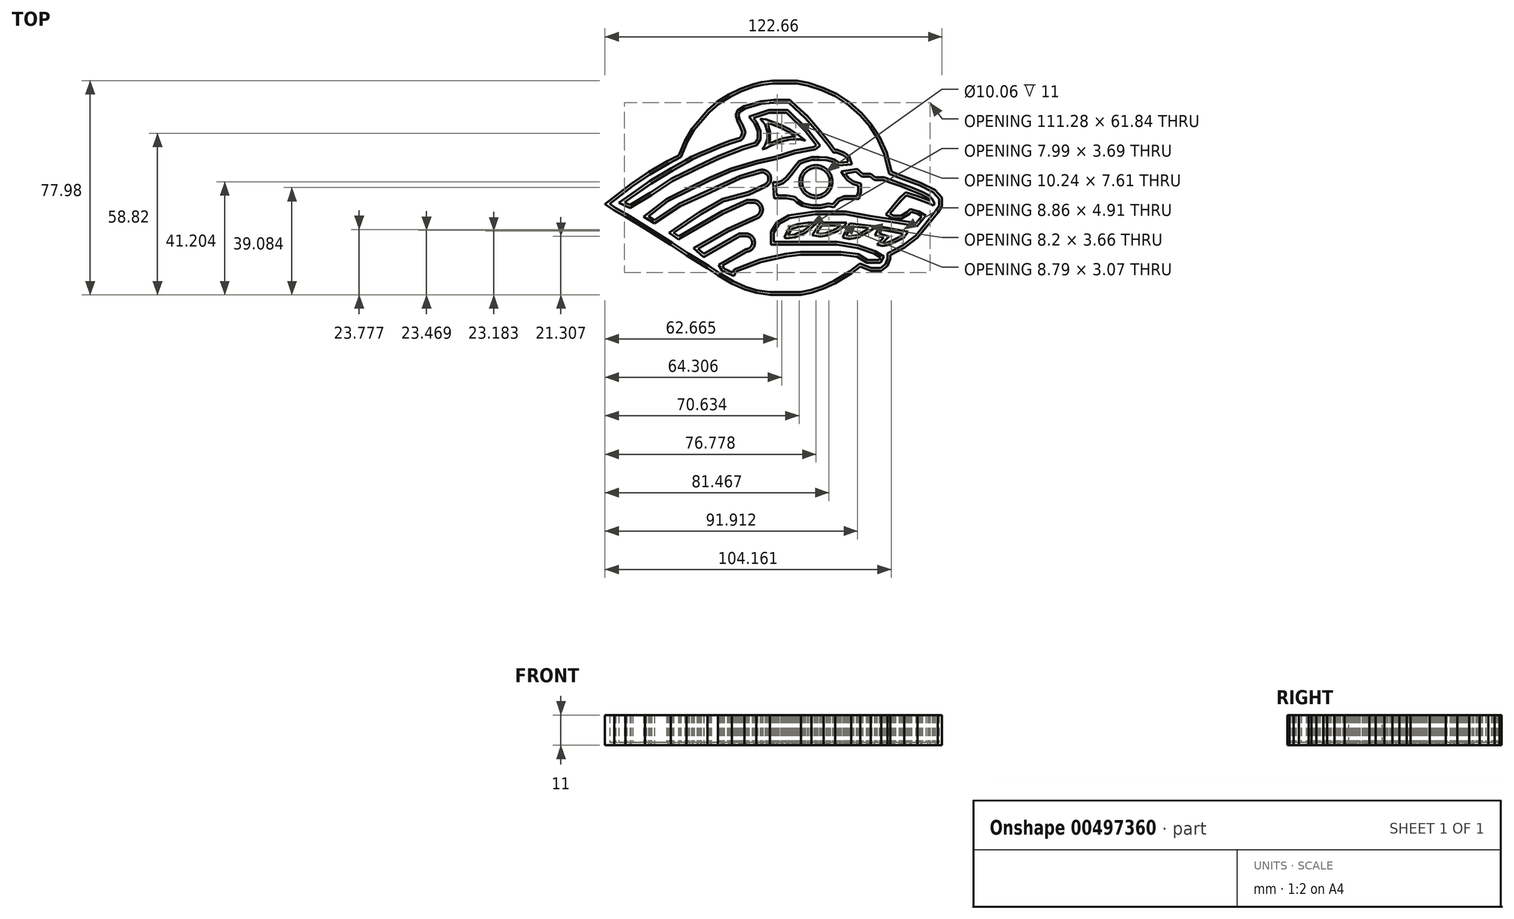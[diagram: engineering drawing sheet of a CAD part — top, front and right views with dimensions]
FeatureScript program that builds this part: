
annotation { "Feature Type Name" : "Feature", "Feature Type Description" : "" }
export const myFeature = defineFeature(function(context is Context, id is Id, definition is map)
    precondition{}
    {
        {
            var Q0;
            Q0=qCreatedBy(makeId("Top.planeOp"),FACE);
            var sketch = newSketch(context, id + "F0", { "sketchPlane" : qUnion([Q0])});
            skLineSegment(sketch, "E0", {"start": v(-64.4, -1.88) * mm, "end": v(-56.05, 4.66) * mm});
            skLineSegment(sketch, "E1", {"start": v(-56.05, 4.66) * mm, "end": v(-49.76, 8.87) * mm});
            skLineSegment(sketch, "E2", {"start": v(-49.76, 8.87) * mm, "end": v(-42.78, 12.9) * mm});
            skLineSegment(sketch, "E3", {"start": v(-42.78, 12.9) * mm, "end": v(-38.45, 15.16) * mm});
            skLineSegment(sketch, "E4", {"start": v(-38.45, 15.16) * mm, "end": v(-36.18, 20.62) * mm});
            skLineSegment(sketch, "E5", {"start": v(-36.18, 20.62) * mm, "end": v(-33.6, 25.09) * mm});
            skLineSegment(sketch, "E6", {"start": v(-33.6, 25.09) * mm, "end": v(-28.15, 31.5) * mm});
            skLineSegment(sketch, "E7", {"start": v(-28.15, 31.5) * mm, "end": v(-24.6, 34.58) * mm});
            skLineSegment(sketch, "E8", {"start": v(-24.6, 34.58) * mm, "end": v(-20.43, 37.2) * mm});
            skLineSegment(sketch, "E9", {"start": v(-20.43, 37.2) * mm, "end": v(-16.4, 39.2) * mm});
            skLineSegment(sketch, "E10", {"start": v(-16.4, 39.2) * mm, "end": v(-11.8, 40.82) * mm});
            skLineSegment(sketch, "E11", {"start": v(-11.8, 40.82) * mm, "end": v(-8.9, 41.51) * mm});
            skLineSegment(sketch, "E12", {"start": v(-8.9, 41.51) * mm, "end": v(-5.07, 42) * mm});
            skLineSegment(sketch, "E13", {"start": v(-5.07, 42) * mm, "end": v(0, 42) * mm});
            skLineSegment(sketch, "E14", {"start": v(0, 42) * mm, "end": v(3.77, 42) * mm});
            skLineSegment(sketch, "E15", {"start": v(3.77, 42) * mm, "end": v(7.58, 41.25) * mm});
            skLineSegment(sketch, "E16", {"start": v(7.58, 41.25) * mm, "end": v(12.68, 39.55) * mm});
            skLineSegment(sketch, "E17", {"start": v(12.68, 39.55) * mm, "end": v(17.83, 37.29) * mm});
            skLineSegment(sketch, "E18", {"start": v(17.83, 37.29) * mm, "end": v(22.37, 34.25) * mm});
            skLineSegment(sketch, "E19", {"start": v(22.37, 34.25) * mm, "end": v(26.64, 30.49) * mm});
            skLineSegment(sketch, "E20", {"start": v(26.64, 30.49) * mm, "end": v(30.21, 26.3) * mm});
            skLineSegment(sketch, "E21", {"start": v(30.21, 26.3) * mm, "end": v(32.91, 22.22) * mm});
            skLineSegment(sketch, "E22", {"start": v(32.91, 22.22) * mm, "end": v(35.46, 16.47) * mm});
            skLineSegment(sketch, "E23", {"start": v(35.46, 16.47) * mm, "end": v(36.78, 11.36) * mm});
            skLineSegment(sketch, "E24", {"start": v(36.78, 11.36) * mm, "end": v(37.36, 9.1) * mm});
            skLineSegment(sketch, "E25", {"start": v(37.36, 9.1) * mm, "end": v(41.44, 7.5) * mm});
            skLineSegment(sketch, "E26", {"start": v(41.44, 7.5) * mm, "end": v(48.44, 4.87) * mm});
            skLineSegment(sketch, "E27", {"start": v(48.44, 4.87) * mm, "end": v(53.32, 2.4) * mm});
            skLineSegment(sketch, "E28", {"start": v(53.32, 2.4) * mm, "end": v(55.56, 0) * mm});
            skLineSegment(sketch, "E29", {"start": v(55.56, 0) * mm, "end": v(55.56, -2.46) * mm});
            skLineSegment(sketch, "E30", {"start": v(55.56, -2.46) * mm, "end": v(54.15, -4.5) * mm});
            skLineSegment(sketch, "E31", {"start": v(54.15, -4.5) * mm, "end": v(49.78, -9.92) * mm});
            skLineSegment(sketch, "E32", {"start": v(49.78, -9.92) * mm, "end": v(46.97, -13.37) * mm});
            skLineSegment(sketch, "E33", {"start": v(46.97, -13.37) * mm, "end": v(42.25, -16.98) * mm});
            skLineSegment(sketch, "E34", {"start": v(42.25, -16.98) * mm, "end": v(36.78, -19.86) * mm});
            skLineSegment(sketch, "E35", {"start": v(36.78, -19.86) * mm, "end": v(36.78, -21.72) * mm});
            skLineSegment(sketch, "E36", {"start": v(36.78, -21.72) * mm, "end": v(35.95, -23.82) * mm});
            skLineSegment(sketch, "E37", {"start": v(35.95, -23.82) * mm, "end": v(34.14, -25.2) * mm});
            skLineSegment(sketch, "E38", {"start": v(34.14, -25.2) * mm, "end": v(30.8, -25.2) * mm});
            skLineSegment(sketch, "E39", {"start": v(30.8, -25.2) * mm, "end": v(26.64, -23.56) * mm});
            skLineSegment(sketch, "E40", {"start": v(26.64, -23.56) * mm, "end": v(22.9, -26.43) * mm});
            skLineSegment(sketch, "E41", {"start": v(22.9, -26.43) * mm, "end": v(17.22, -29.9) * mm});
            skLineSegment(sketch, "E42", {"start": v(17.22, -29.9) * mm, "end": v(13.15, -31.77) * mm});
            skLineSegment(sketch, "E43", {"start": v(13.15, -31.77) * mm, "end": v(8.8, -33.2) * mm});
            skLineSegment(sketch, "E44", {"start": v(8.8, -33.2) * mm, "end": v(5.08, -33.98) * mm});
            skLineSegment(sketch, "E45", {"start": v(5.08, -33.98) * mm, "end": v(3.36, -33.98) * mm});
            skLineSegment(sketch, "E46", {"start": v(3.36, -33.98) * mm, "end": v(0, -33.98) * mm});
            skLineSegment(sketch, "E47", {"start": v(0, -33.98) * mm, "end": v(-6.07, -33.98) * mm});
            skLineSegment(sketch, "E48", {"start": v(-6.07, -33.98) * mm, "end": v(-10.85, -33.27) * mm});
            skLineSegment(sketch, "E49", {"start": v(-10.85, -33.27) * mm, "end": v(-15, -32.05) * mm});
            skLineSegment(sketch, "E50", {"start": v(-15, -32.05) * mm, "end": v(-19.43, -30.05) * mm});
            skLineSegment(sketch, "E51", {"start": v(-19.43, -30.05) * mm, "end": v(-24.43, -27.05) * mm});
            skLineSegment(sketch, "E52", {"start": v(-24.43, -27.05) * mm, "end": v(-28.28, -24.48) * mm});
            skLineSegment(sketch, "E53", {"start": v(-28.28, -24.48) * mm, "end": v(-35.86, -19.84) * mm});
            skLineSegment(sketch, "E54", {"start": v(-35.86, -19.84) * mm, "end": v(-41.56, -16.03) * mm});
            skLineSegment(sketch, "E55", {"start": v(-41.56, -16.03) * mm, "end": v(-51.02, -10.02) * mm});
            skLineSegment(sketch, "E56", {"start": v(-51.02, -10.02) * mm, "end": v(-58.15, -5.7) * mm});
            skLineSegment(sketch, "E57", {"start": v(-58.15, -5.7) * mm, "end": v(-62.23, -3.37) * mm});
            skLineSegment(sketch, "E58", {"start": v(-62.23, -3.37) * mm, "end": v(-64.4, -1.88) * mm});
            skLineSegment(sketch, "E59", {"start": v(-56.97, -3.37) * mm, "end": v(-49.14, 1.4) * mm});
            skPoint(sketch, "E59.endSnap0", {"position": v(-60.23, 1.4) * mm});
            skLineSegment(sketch, "E60", {"start": v(-49.14, 1.4) * mm, "end": v(-41.56, 6.47) * mm});
            skLineSegment(sketch, "E61", {"start": v(-41.56, 6.47) * mm, "end": v(-32.22, 11.03) * mm});
            skLineSegment(sketch, "E62", {"start": v(-32.22, 11.03) * mm, "end": v(-24.43, 14.66) * mm});
            skLineSegment(sketch, "E63", {"start": v(-24.43, 14.66) * mm, "end": v(-15.86, 18.02) * mm});
            skLineSegment(sketch, "E64", {"start": v(-15.86, 18.02) * mm, "end": v(-10.85, 19.56) * mm});
            skLineSegment(sketch, "E65", {"start": v(-10.85, 19.56) * mm, "end": v(-9.56, 21.7) * mm});
            skLineSegment(sketch, "E66", {"start": v(-9.56, 21.7) * mm, "end": v(-9.56, 24.73) * mm});
            skLineSegment(sketch, "E67", {"start": v(-9.56, 24.73) * mm, "end": v(-10.85, 27.94) * mm});
            skLineSegment(sketch, "E68", {"start": v(-10.85, 27.94) * mm, "end": v(-12.02, 29.44) * mm});
            skLineSegment(sketch, "E69", {"start": v(-12.02, 29.44) * mm, "end": v(-6.35, 31.3) * mm});
            skLineSegment(sketch, "E70", {"start": v(-6.35, 31.3) * mm, "end": v(-4.12, 31.3) * mm});
            skLineSegment(sketch, "E71", {"start": v(-4.12, 31.3) * mm, "end": v(0, 31.3) * mm});
            skLineSegment(sketch, "E72", {"start": v(0, 31.3) * mm, "end": v(6.79, 24.73) * mm});
            skLineSegment(sketch, "E73", {"start": v(6.79, 24.73) * mm, "end": v(10.84, 19.56) * mm});
            skLineSegment(sketch, "E74", {"start": v(10.84, 19.56) * mm, "end": v(9.97, 18.88) * mm});
            skLineSegment(sketch, "E75", {"start": v(9.97, 18.88) * mm, "end": v(2.87, 17.6) * mm});
            skLineSegment(sketch, "E76", {"start": v(2.87, 17.6) * mm, "end": v(-4.12, 15.36) * mm});
            skLineSegment(sketch, "E77", {"start": v(-4.12, 15.36) * mm, "end": v(-10.85, 13.82) * mm});
            skLineSegment(sketch, "E78", {"start": v(-10.85, 13.82) * mm, "end": v(-20.33, 11.03) * mm});
            skLineSegment(sketch, "E79", {"start": v(-20.33, 11.03) * mm, "end": v(-28.28, 7.53) * mm});
            skLineSegment(sketch, "E80", {"start": v(-28.28, 7.53) * mm, "end": v(-35.86, 3.9) * mm});
            skLineSegment(sketch, "E81", {"start": v(-35.86, 3.9) * mm, "end": v(-43.68, 0) * mm});
            skLineSegment(sketch, "E82", {"start": v(-43.68, 0) * mm, "end": v(-52.05, -6.54) * mm});
            skLineSegment(sketch, "E83", {"start": v(-52.05, -6.54) * mm, "end": v(-48.07, -8.96) * mm});
            skLineSegment(sketch, "E84", {"start": v(-48.07, -8.96) * mm, "end": v(-38.7, -2.68) * mm});
            skLineSegment(sketch, "E85", {"start": v(-38.7, -2.68) * mm, "end": v(-29.7, 1.4) * mm});
            skLineSegment(sketch, "E86", {"start": v(-29.7, 1.4) * mm, "end": v(-16.7, 7.4) * mm});
            skLineSegment(sketch, "E87", {"start": v(-16.7, 7.4) * mm, "end": v(-9.56, 9.49) * mm});
            skArc(sketch, "E88", {"start": v(-7.9, 5.3) * mm, "mid": v(-6.81, 8.15) * mm, "end": v(-9.56, 9.49) * mm});
            skLineSegment(sketch, "E89", {"start": v(-7.9, 5.3) * mm, "end": v(-14, 2.48) * mm});
            skLineSegment(sketch, "E90", {"start": v(-14, 2.48) * mm, "end": v(-23.41, 0) * mm});
            skLineSegment(sketch, "E91", {"start": v(-23.41, 0) * mm, "end": v(-31.85, -4.87) * mm});
            skLineSegment(sketch, "E92", {"start": v(-31.85, -4.87) * mm, "end": v(-42.85, -12.32) * mm});
            skLineSegment(sketch, "E93", {"start": v(-42.85, -12.32) * mm, "end": v(-39.35, -14.84) * mm});
            skLineSegment(sketch, "E94", {"start": v(-39.35, -14.84) * mm, "end": v(-31.7, -10.43) * mm});
            skLineSegment(sketch, "E95", {"start": v(-31.7, -10.43) * mm, "end": v(-23.02, -5.42) * mm});
            skLineSegment(sketch, "E96", {"start": v(-23.02, -5.42) * mm, "end": v(-14.3, -1.4) * mm});
            skLineSegment(sketch, "E97", {"start": v(-14.3, -1.4) * mm, "end": v(-12.23, -1.4) * mm});
            skArc(sketch, "E98", {"start": v(-10.94, -6.17) * mm, "mid": v(-9.75, -3.3) * mm, "end": v(-12.23, -1.4) * mm});
            skPoint(sketch, "E98.startSnap0", {"position": v(-10.94, 3.89) * mm});
            skLineSegment(sketch, "E99", {"start": v(-10.94, -6.17) * mm, "end": v(-21.6, -10.93) * mm});
            skLineSegment(sketch, "E100", {"start": v(-21.6, -10.93) * mm, "end": v(-33.9, -18.02) * mm});
            skLineSegment(sketch, "E101", {"start": v(-33.9, -18.02) * mm, "end": v(-30.26, -21.27) * mm});
            skLineSegment(sketch, "E102", {"start": v(-30.26, -21.27) * mm, "end": v(-24.16, -17.75) * mm});
            skLineSegment(sketch, "E103", {"start": v(-24.16, -17.75) * mm, "end": v(-16.98, -13.61) * mm});
            skLineSegment(sketch, "E104", {"start": v(-16.98, -13.61) * mm, "end": v(-14.88, -13.61) * mm});
            skArc(sketch, "E105", {"start": v(-14.88, -18.34) * mm, "mid": v(-12.52, -15.98) * mm, "end": v(-14.88, -13.61) * mm});
            skLineSegment(sketch, "E106", {"start": v(-14.88, -18.34) * mm, "end": v(-24.7, -24) * mm});
            skLineSegment(sketch, "E107", {"start": v(-24.7, -24) * mm, "end": v(-23.43, -26.2) * mm});
            skLineSegment(sketch, "E108", {"start": v(-23.43, -26.2) * mm, "end": v(-14.88, -30.05) * mm});
            skLineSegment(sketch, "E109", {"start": v(-14.88, -30.05) * mm, "end": v(-8.45, -32.05) * mm});
            skLineSegment(sketch, "E110", {"start": v(-8.45, -32.05) * mm, "end": v(-2.72, -32.05) * mm});
            skLineSegment(sketch, "E111", {"start": v(-2.72, -32.05) * mm, "end": v(0, -32.05) * mm});
            skLineSegment(sketch, "E112", {"start": v(0, -32.05) * mm, "end": v(6.1, -32.05) * mm});
            skLineSegment(sketch, "E113", {"start": v(6.1, -32.05) * mm, "end": v(13.7, -28.6) * mm});
            skLineSegment(sketch, "E114", {"start": v(13.7, -28.6) * mm, "end": v(22.13, -23.75) * mm});
            skLineSegment(sketch, "E115", {"start": v(22.13, -23.75) * mm, "end": v(25.67, -21.13) * mm});
            skLineSegment(sketch, "E116", {"start": v(25.67, -21.13) * mm, "end": v(29.22, -23.27) * mm});
            skLineSegment(sketch, "E117", {"start": v(29.22, -23.27) * mm, "end": v(34.2, -23.27) * mm});
            skLineSegment(sketch, "E118", {"start": v(34.2, -23.27) * mm, "end": v(35.52, -21.06) * mm});
            skLineSegment(sketch, "E119", {"start": v(35.52, -21.06) * mm, "end": v(32.31, -19.14) * mm});
            skLineSegment(sketch, "E120", {"start": v(32.31, -19.14) * mm, "end": v(26.22, -16.94) * mm});
            skLineSegment(sketch, "E121", {"start": v(26.22, -16.94) * mm, "end": v(18.4, -15.68) * mm});
            skLineSegment(sketch, "E122", {"start": v(18.4, -15.68) * mm, "end": v(9.3, -15.68) * mm});
            skLineSegment(sketch, "E123", {"start": v(9.3, -15.68) * mm, "end": v(1.34, -15.68) * mm});
            skLineSegment(sketch, "E124", {"start": v(1.34, -15.68) * mm, "end": v(-2.44, -15.68) * mm});
            skLineSegment(sketch, "E125", {"start": v(-2.44, -15.68) * mm, "end": v(-4.68, -15.68) * mm});
            skLineSegment(sketch, "E126", {"start": v(-4.68, -15.68) * mm, "end": v(-4.68, -12.32) * mm});
            skLineSegment(sketch, "E127", {"start": v(-4.68, -12.32) * mm, "end": v(-2.82, -9.24) * mm});
            skLineSegment(sketch, "E128", {"start": v(-2.82, -9.24) * mm, "end": v(1.1, -6.98) * mm});
            skLineSegment(sketch, "E129", {"start": v(1.1, -6.98) * mm, "end": v(10.43, -5.61) * mm});
            skLineSegment(sketch, "E130", {"start": v(10.43, -5.61) * mm, "end": v(21.33, -5.61) * mm});
            skLineSegment(sketch, "E131", {"start": v(21.33, -5.61) * mm, "end": v(30.28, -7.29) * mm});
            skLineSegment(sketch, "E132", {"start": v(30.28, -7.29) * mm, "end": v(40.49, -8.83) * mm});
            skLineSegment(sketch, "E133", {"start": v(40.49, -8.83) * mm, "end": v(47.53, -9.92) * mm});
            skLineSegment(sketch, "E134", {"start": v(47.53, -9.92) * mm, "end": v(50.66, -6.1) * mm});
            skLineSegment(sketch, "E135", {"start": v(50.66, -6.1) * mm, "end": v(48.12, -4.57) * mm});
            skLineSegment(sketch, "E136", {"start": v(48.12, -4.57) * mm, "end": v(44.94, -3.67) * mm});
            skLineSegment(sketch, "E137", {"start": v(44.94, -3.67) * mm, "end": v(44.02, -4.8) * mm});
            skLineSegment(sketch, "E138", {"start": v(44.02, -4.8) * mm, "end": v(41.71, -6.13) * mm});
            skLineSegment(sketch, "E139", {"start": v(41.71, -6.13) * mm, "end": v(40.5, -6.13) * mm});
            skLineSegment(sketch, "E140", {"start": v(40.5, -6.13) * mm, "end": v(38.99, -6.13) * mm});
            skLineSegment(sketch, "E141", {"start": v(38.99, -6.13) * mm, "end": v(37.65, -5.43) * mm});
            skLineSegment(sketch, "E142", {"start": v(37.65, -5.43) * mm, "end": v(41.71, -0.66) * mm});
            skLineSegment(sketch, "E143", {"start": v(41.71, -0.66) * mm, "end": v(43.6, 1.27) * mm});
            skLineSegment(sketch, "E144", {"start": v(43.6, 1.27) * mm, "end": v(47.45, 0) * mm});
            skLineSegment(sketch, "E145", {"start": v(47.45, 0) * mm, "end": v(51.89, -1.66) * mm});
            skLineSegment(sketch, "E146", {"start": v(51.89, -1.66) * mm, "end": v(53.52, -2.46) * mm});
            skLineSegment(sketch, "E147", {"start": v(53.52, -2.46) * mm, "end": v(53.9, -1.66) * mm});
            skLineSegment(sketch, "E148", {"start": v(53.9, -1.66) * mm, "end": v(52.95, 0) * mm});
            skLineSegment(sketch, "E149", {"start": v(52.95, 0) * mm, "end": v(51.89, 1.16) * mm});
            skLineSegment(sketch, "E150", {"start": v(51.89, 1.16) * mm, "end": v(49.39, 2.5) * mm});
            skLineSegment(sketch, "E151", {"start": v(49.39, 2.5) * mm, "end": v(45.53, 4.1) * mm});
            skLineSegment(sketch, "E152", {"start": v(45.53, 4.1) * mm, "end": v(41.71, 5.56) * mm});
            skLineSegment(sketch, "E153", {"start": v(41.71, 5.56) * mm, "end": v(38, 6.89) * mm});
            skLineSegment(sketch, "E154", {"start": v(38, 6.89) * mm, "end": v(35.4, 7.82) * mm});
            skLineSegment(sketch, "E155", {"start": v(35.4, 7.82) * mm, "end": v(34.67, 12.55) * mm});
            skLineSegment(sketch, "E156", {"start": v(34.67, 12.55) * mm, "end": v(33.2, 16.88) * mm});
            skLineSegment(sketch, "E157", {"start": v(33.2, 16.88) * mm, "end": v(31.56, 20.94) * mm});
            skPoint(sketch, "E157.endSnap0", {"position": v(31.56, 24.27) * mm});
            skLineSegment(sketch, "E158", {"start": v(31.56, 20.94) * mm, "end": v(28.02, 26.3) * mm});
            skLineSegment(sketch, "E159", {"start": v(28.02, 26.3) * mm, "end": v(24.44, 30.49) * mm});
            skLineSegment(sketch, "E160", {"start": v(24.44, 30.49) * mm, "end": v(18.81, 34.42) * mm});
            skLineSegment(sketch, "E161", {"start": v(18.81, 34.42) * mm, "end": v(11.34, 38.26) * mm});
            skLineSegment(sketch, "E162", {"start": v(11.34, 38.26) * mm, "end": v(5.52, 39.72) * mm});
            skLineSegment(sketch, "E163", {"start": v(5.52, 39.72) * mm, "end": v(0, 40.65) * mm});
            skLineSegment(sketch, "E164", {"start": v(0, 40.65) * mm, "end": v(-7.35, 39.72) * mm});
            skLineSegment(sketch, "E165", {"start": v(-7.35, 39.72) * mm, "end": v(-13.68, 38.37) * mm});
            skLineSegment(sketch, "E166", {"start": v(-13.68, 38.37) * mm, "end": v(-18.24, 36.5) * mm});
            skLineSegment(sketch, "E167", {"start": v(-18.24, 36.5) * mm, "end": v(-23.7, 33.07) * mm});
            skLineSegment(sketch, "E168", {"start": v(-23.7, 33.07) * mm, "end": v(-28, 28.95) * mm});
            skLineSegment(sketch, "E169", {"start": v(-28, 28.95) * mm, "end": v(-31.22, 25) * mm});
            skLineSegment(sketch, "E170", {"start": v(-31.22, 25) * mm, "end": v(-34.45, 19.63) * mm});
            skLineSegment(sketch, "E171", {"start": v(-34.45, 19.63) * mm, "end": v(-36.78, 13.99) * mm});
            skLineSegment(sketch, "E172", {"start": v(-36.78, 13.99) * mm, "end": v(-41.97, 11.12) * mm});
            skLineSegment(sketch, "E173", {"start": v(-41.97, 11.12) * mm, "end": v(-49.86, 6.37) * mm});
            skLineSegment(sketch, "E174", {"start": v(-49.86, 6.37) * mm, "end": v(-56.94, 1.44) * mm});
            skLineSegment(sketch, "E175", {"start": v(-56.94, 1.44) * mm, "end": v(-61.06, -1.43) * mm});
            skLineSegment(sketch, "E176", {"start": v(-61.06, -1.43) * mm, "end": v(-56.97, -3.37) * mm});
            skLineSegment(sketch, "E177", {"start": v(-3.57, 1.24) * mm, "end": v(0, 1.24) * mm});
            skLineSegment(sketch, "E178", {"start": v(0, 1.24) * mm, "end": v(2.35, 0.8) * mm});
            skLineSegment(sketch, "E179", {"start": v(2.35, 0.8) * mm, "end": v(3.09, 0.66) * mm});
            skLineSegment(sketch, "E180", {"start": v(3.09, 0.66) * mm, "end": v(4.3, -0.56) * mm});
            skLineSegment(sketch, "E181", {"start": v(4.3, -0.56) * mm, "end": v(6.1, -1.7) * mm});
            skLineSegment(sketch, "E182", {"start": v(6.1, -1.7) * mm, "end": v(7.7, -2.01) * mm});
            skLineSegment(sketch, "E183", {"start": v(7.7, -2.01) * mm, "end": v(9.3, -2.3) * mm});
            skLineSegment(sketch, "E184", {"start": v(9.3, -2.3) * mm, "end": v(12.3, -2.3) * mm});
            skLineSegment(sketch, "E185", {"start": v(12.3, -2.3) * mm, "end": v(15.24, -1.7) * mm});
            skLineSegment(sketch, "E186", {"start": v(15.24, -1.7) * mm, "end": v(16.84, -2) * mm});
            skLineSegment(sketch, "E187", {"start": v(16.84, -2) * mm, "end": v(18.57, 0) * mm});
            skLineSegment(sketch, "E188", {"start": v(18.57, 0) * mm, "end": v(20.92, 0.96) * mm});
            skLineSegment(sketch, "E189", {"start": v(20.92, 0.96) * mm, "end": v(23.05, 0.96) * mm});
            skLineSegment(sketch, "E190", {"start": v(23.05, 0.96) * mm, "end": v(25.54, 0.96) * mm});
            skLineSegment(sketch, "E191", {"start": v(25.54, 0.96) * mm, "end": v(26.05, 2.53) * mm});
            skLineSegment(sketch, "E192", {"start": v(26.05, 2.53) * mm, "end": v(26.05, 4.78) * mm});
            skLineSegment(sketch, "E193", {"start": v(26.05, 4.78) * mm, "end": v(24.01, 5.37) * mm});
            skLineSegment(sketch, "E194", {"start": v(24.01, 5.37) * mm, "end": v(21.98, 6.85) * mm});
            skLineSegment(sketch, "E195", {"start": v(21.98, 6.85) * mm, "end": v(20.84, 8.29) * mm});
            skLineSegment(sketch, "E196", {"start": v(20.84, 8.29) * mm, "end": v(19.78, 9.98) * mm});
            skLineSegment(sketch, "E197", {"start": v(19.78, 9.98) * mm, "end": v(18.77, 12.1) * mm});
            skLineSegment(sketch, "E198", {"start": v(18.77, 12.1) * mm, "end": v(17.03, 13.4) * mm});
            skLineSegment(sketch, "E199", {"start": v(17.03, 13.4) * mm, "end": v(14.5, 14.09) * mm});
            skLineSegment(sketch, "E200", {"start": v(14.5, 14.09) * mm, "end": v(11.95, 14.13) * mm});
            skLineSegment(sketch, "E201", {"start": v(11.95, 14.13) * mm, "end": v(9.25, 14.13) * mm});
            skLineSegment(sketch, "E202", {"start": v(9.25, 14.13) * mm, "end": v(6.5, 13.37) * mm});
            skLineSegment(sketch, "E203", {"start": v(6.5, 13.37) * mm, "end": v(5.02, 12.77) * mm});
            skLineSegment(sketch, "E204", {"start": v(5.02, 12.77) * mm, "end": v(3.58, 11.04) * mm});
            skLineSegment(sketch, "E205", {"start": v(3.58, 11.04) * mm, "end": v(1.84, 8.71) * mm});
            skLineSegment(sketch, "E206", {"start": v(1.84, 8.71) * mm, "end": v(0.36, 7.02) * mm});
            skLineSegment(sketch, "E207", {"start": v(0.36, 7.02) * mm, "end": v(-1.29, 5.7) * mm});
            skLineSegment(sketch, "E208", {"start": v(-1.29, 5.7) * mm, "end": v(-2.9, 5.03) * mm});
            skLineSegment(sketch, "E209", {"start": v(-2.9, 5.03) * mm, "end": v(-3.83, 5.03) * mm});
            skLineSegment(sketch, "E210", {"start": v(-3.83, 5.03) * mm, "end": v(-3.57, 1.24) * mm});
            skLineSegment(sketch, "E211", {"start": v(1.1, -10.1) * mm, "end": v(-0.9, -13.97) * mm});
            skLineSegment(sketch, "E212", {"start": v(-0.9, -13.97) * mm, "end": v(0, -14.44) * mm});
            skLineSegment(sketch, "E213", {"start": v(0, -14.44) * mm, "end": v(3.09, -14) * mm});
            skLineSegment(sketch, "E214", {"start": v(3.09, -14) * mm, "end": v(6.83, -12.31) * mm});
            skLineSegment(sketch, "E215", {"start": v(6.83, -12.31) * mm, "end": v(9.3, -10.32) * mm});
            skLineSegment(sketch, "E216", {"start": v(9.3, -10.32) * mm, "end": v(11.03, -8.67) * mm});
            skLineSegment(sketch, "E217", {"start": v(11.03, -8.67) * mm, "end": v(7.82, -8.67) * mm});
            skLineSegment(sketch, "E218", {"start": v(7.82, -8.67) * mm, "end": v(4.27, -9.19) * mm});
            skLineSegment(sketch, "E219", {"start": v(4.27, -9.19) * mm, "end": v(1.1, -10.1) * mm});
            skLineSegment(sketch, "E220", {"start": v(9.3, -13.2) * mm, "end": v(12.3, -8.67) * mm});
            skLineSegment(sketch, "E221", {"start": v(12.3, -8.67) * mm, "end": v(18.4, -8.67) * mm});
            skLineSegment(sketch, "E222", {"start": v(18.4, -8.67) * mm, "end": v(21.86, -8.67) * mm});
            skLineSegment(sketch, "E223", {"start": v(21.86, -8.67) * mm, "end": v(20.87, -10.1) * mm});
            skLineSegment(sketch, "E224", {"start": v(20.87, -10.1) * mm, "end": v(18.4, -11.87) * mm});
            skLineSegment(sketch, "E225", {"start": v(18.4, -11.87) * mm, "end": v(14.57, -13.42) * mm});
            skLineSegment(sketch, "E226", {"start": v(14.57, -13.42) * mm, "end": v(12.3, -13.75) * mm});
            skLineSegment(sketch, "E227", {"start": v(12.3, -13.75) * mm, "end": v(9.3, -13.2) * mm});
            skLineSegment(sketch, "E228", {"start": v(22.97, -8.89) * mm, "end": v(32.8, -10.1) * mm});
            skLineSegment(sketch, "E229", {"start": v(32.8, -10.1) * mm, "end": v(29.5, -12.2) * mm});
            skLineSegment(sketch, "E230", {"start": v(29.5, -12.2) * mm, "end": v(25.95, -14.2) * mm});
            skLineSegment(sketch, "E231", {"start": v(25.95, -14.2) * mm, "end": v(22.9, -14.64) * mm});
            skLineSegment(sketch, "E232", {"start": v(22.9, -14.64) * mm, "end": v(20.5, -14.2) * mm});
            skLineSegment(sketch, "E233", {"start": v(20.5, -14.2) * mm, "end": v(20.69, -13.2) * mm});
            skLineSegment(sketch, "E234", {"start": v(20.69, -13.2) * mm, "end": v(22.97, -8.89) * mm});
            skLineSegment(sketch, "E235", {"start": v(32.15, -13.2) * mm, "end": v(33.91, -10.1) * mm});
            skLineSegment(sketch, "E236", {"start": v(33.91, -10.1) * mm, "end": v(40.8, -11.4) * mm});
            skLineSegment(sketch, "E237", {"start": v(40.8, -11.4) * mm, "end": v(44.25, -12.04) * mm});
            skLineSegment(sketch, "E238", {"start": v(44.25, -12.04) * mm, "end": v(42.65, -14.2) * mm});
            skLineSegment(sketch, "E239", {"start": v(42.65, -14.2) * mm, "end": v(39.66, -15.68) * mm});
            skLineSegment(sketch, "E240", {"start": v(39.66, -15.68) * mm, "end": v(37, -16.85) * mm});
            skLineSegment(sketch, "E241", {"start": v(37, -16.85) * mm, "end": v(35, -17.14) * mm});
            skLineSegment(sketch, "E242", {"start": v(35, -17.14) * mm, "end": v(32.88, -16.74) * mm});
            skLineSegment(sketch, "E243", {"start": v(32.88, -16.74) * mm, "end": v(35.35, -14.2) * mm});
            skLineSegment(sketch, "E244", {"start": v(35.35, -14.2) * mm, "end": v(32.15, -13.2) * mm});
            skCircle(sketch, "E245", {"center": v(10.68, 6.22) * mm, "radius": 6.03 * mm});
            skLineSegment(sketch, "E246", {"start": v(-18.36, -26.52) * mm, "end": v(-9.27, -22.98) * mm});
            skLineSegment(sketch, "E247", {"start": v(-9.27, -22.98) * mm, "end": v(0, -20.97) * mm});
            skLineSegment(sketch, "E248", {"start": v(5.06, -20.36) * mm, "end": v(0, -20.97) * mm});
            skLineSegment(sketch, "E249", {"start": v(5.06, -20.36) * mm, "end": v(12.15, -20.36) * mm});
            skLineSegment(sketch, "E250", {"start": v(12.15, -20.36) * mm, "end": v(19.7, -20.36) * mm});
            skLineSegment(sketch, "E251", {"start": v(19.7, -20.36) * mm, "end": v(25.67, -21.13) * mm});
            skLineSegment(sketch, "E252", {"start": v(35.4, 7.82) * mm, "end": v(32.34, 7.82) * mm});
            skLineSegment(sketch, "E253", {"start": v(32.34, 7.82) * mm, "end": v(30.64, 9.08) * mm});
            skLineSegment(sketch, "E254", {"start": v(30.64, 9.08) * mm, "end": v(27.71, 9.08) * mm});
            skLineSegment(sketch, "E255", {"start": v(27.71, 9.08) * mm, "end": v(25.67, 10.93) * mm});
            skLineSegment(sketch, "E256", {"start": v(25.67, 10.93) * mm, "end": v(23.7, 12.47) * mm});
            skLineSegment(sketch, "E257", {"start": v(23.7, 12.47) * mm, "end": v(22.8, 15.54) * mm});
            skLineSegment(sketch, "E258", {"start": v(22.8, 15.54) * mm, "end": v(20.92, 16.78) * mm});
            skLineSegment(sketch, "E259", {"start": v(20.92, 16.78) * mm, "end": v(18.31, 17.86) * mm});
            skLineSegment(sketch, "E260", {"start": v(18.31, 17.86) * mm, "end": v(17.55, 17.86) * mm});
            skLineSegment(sketch, "E261", {"start": v(17.55, 17.86) * mm, "end": v(15.91, 20.1) * mm});
            skLineSegment(sketch, "E262", {"start": v(15.91, 20.1) * mm, "end": v(12.1, 24.86) * mm});
            skLineSegment(sketch, "E263", {"start": v(12.1, 24.86) * mm, "end": v(7.47, 30.17) * mm});
            skLineSegment(sketch, "E264", {"start": v(7.47, 30.17) * mm, "end": v(3.66, 33.64) * mm});
            skLineSegment(sketch, "E265", {"start": v(3.66, 33.64) * mm, "end": v(1.2, 36.02) * mm});
            skLineSegment(sketch, "E266", {"start": v(1.2, 36.02) * mm, "end": v(-0.9, 36.02) * mm});
            skLineSegment(sketch, "E267", {"start": v(-0.9, 36.02) * mm, "end": v(-4.72, 36.02) * mm});
            skLineSegment(sketch, "E268", {"start": v(-4.72, 36.02) * mm, "end": v(-9.35, 35.55) * mm});
            skLineSegment(sketch, "E269", {"start": v(-9.35, 35.55) * mm, "end": v(-15.47, 33.78) * mm});
            skLineSegment(sketch, "E270", {"start": v(-15.47, 33.78) * mm, "end": v(-17.92, 32.21) * mm});
            skLineSegment(sketch, "E271", {"start": v(-17.92, 32.21) * mm, "end": v(-18.54, 30.37) * mm});
            skLineSegment(sketch, "E272", {"start": v(-18.54, 30.37) * mm, "end": v(-17.92, 28.26) * mm});
            skLineSegment(sketch, "E273", {"start": v(-17.92, 28.26) * mm, "end": v(-16.83, 26.15) * mm});
            skLineSegment(sketch, "E274", {"start": v(-16.83, 26.15) * mm, "end": v(-16.09, 24.18) * mm});
            skLineSegment(sketch, "E275", {"start": v(-16.09, 24.18) * mm, "end": v(-16.56, 22.68) * mm});
            skLineSegment(sketch, "E276", {"start": v(-16.56, 22.68) * mm, "end": v(-17.17, 22.14) * mm});
            skLineSegment(sketch, "E277", {"start": v(-17.17, 22.14) * mm, "end": v(-20.58, 21.11) * mm});
            skLineSegment(sketch, "E278", {"start": v(-20.58, 21.11) * mm, "end": v(-24.19, 19.75) * mm});
            skLineSegment(sketch, "E279", {"start": v(-24.19, 19.75) * mm, "end": v(-27.8, 18.25) * mm});
            skLineSegment(sketch, "E280", {"start": v(-27.8, 18.25) * mm, "end": v(-31.54, 16.76) * mm});
            skLineSegment(sketch, "E281", {"start": v(-31.54, 16.76) * mm, "end": v(-34.6, 15.26) * mm});
            skLineSegment(sketch, "E282", {"start": v(-34.6, 15.26) * mm, "end": v(-36.78, 13.99) * mm});
            skLineSegment(sketch, "E283", {"start": v(-8.85, 17.93) * mm, "end": v(-7.88, 19.57) * mm});
            skLineSegment(sketch, "E284", {"start": v(-7.88, 19.57) * mm, "end": v(-7.03, 21.75) * mm});
            skLineSegment(sketch, "E285", {"start": v(-7.03, 21.75) * mm, "end": v(-7.03, 24.3) * mm});
            skLineSegment(sketch, "E286", {"start": v(-7.03, 24.3) * mm, "end": v(-7.82, 27.15) * mm});
            skLineSegment(sketch, "E287", {"start": v(-7.82, 27.15) * mm, "end": v(-9.7, 29.22) * mm});
            skLineSegment(sketch, "E288", {"start": v(-9.7, 29.22) * mm, "end": v(-7.51, 28.91) * mm});
            skLineSegment(sketch, "E289", {"start": v(-7.51, 28.91) * mm, "end": v(-5.09, 28.06) * mm});
            skLineSegment(sketch, "E290", {"start": v(-5.09, 28.06) * mm, "end": v(-1.75, 26.8) * mm});
            skLineSegment(sketch, "E291", {"start": v(-1.75, 26.8) * mm, "end": v(1.28, 25.21) * mm});
            skLineSegment(sketch, "E292", {"start": v(1.28, 25.21) * mm, "end": v(4.44, 23.09) * mm});
            skLineSegment(sketch, "E293", {"start": v(4.44, 23.09) * mm, "end": v(6.87, 21.15) * mm});
            skLineSegment(sketch, "E294", {"start": v(6.87, 21.15) * mm, "end": v(4.8, 21.63) * mm});
            skLineSegment(sketch, "E295", {"start": v(4.8, 21.63) * mm, "end": v(2.32, 21.63) * mm});
            skLineSegment(sketch, "E296", {"start": v(2.32, 21.63) * mm, "end": v(0.37, 21.38) * mm});
            skLineSegment(sketch, "E297", {"start": v(0.37, 21.38) * mm, "end": v(-1.1, 21.02) * mm});
            skLineSegment(sketch, "E298", {"start": v(-1.1, 21.02) * mm, "end": v(-3.11, 20.4) * mm});
            skLineSegment(sketch, "E299", {"start": v(-3.11, 20.4) * mm, "end": v(-5.65, 19.4) * mm});
            skLineSegment(sketch, "E300", {"start": v(-5.65, 19.4) * mm, "end": v(-7.63, 18.42) * mm});
            skLineSegment(sketch, "E301", {"start": v(-7.63, 18.42) * mm, "end": v(-8.85, 17.93) * mm});
            skLineSegment(sketch, "E302", {"start": v(-18.36, -26.52) * mm, "end": v(-19.15, -28.12) * mm});
            skLineSegment(sketch, "E303", {"start": v(25.67, 10.93) * mm, "end": v(19.78, 9.98) * mm});
            skLineSegment(sketch, "E304", {"start": v(23.7, 12.47) * mm, "end": v(18.77, 12.1) * mm});
            skLineSegment(sketch, "E305", {"start": v(10.43, -5.61) * mm, "end": v(15.24, -1.7) * mm});
            skLineSegment(sketch, "E306", {"start": v(21.33, -5.61) * mm, "end": v(20.92, 0.96) * mm});
            skLineSegment(sketch, "E307.bottom", {"start": v(-65.82, 48.1) * mm, "end": v(68.76, 48.1) * mm});
            skLineSegment(sketch, "E307.top", {"start": v(-65.82, -43.57) * mm, "end": v(68.76, -43.57) * mm});
            skLineSegment(sketch, "E307.left", {"start": v(-65.82, 48.1) * mm, "end": v(-65.82, -43.57) * mm});
            skLineSegment(sketch, "E307.right", {"start": v(68.76, 48.1) * mm, "end": v(68.76, -43.57) * mm});
            skSolve(sketch);
        }
        {
            var Q0;
            Q0=makeQuery(id+"F0.imprint","IMPRINT",FACE,{"disambiguationData":[TD([[makeQuery(id+"F0.imprint","IMPRINT",EDGE,{"derivedFrom":sQuery(id+"F0.wireOp",EDGE,"E0")}),-1.0]])]});
            var Q1;
            Q1=makeQuery(id+"F0.imprint","IMPRINT",FACE,{"disambiguationData":[TD([[makeQuery(id+"F0.imprint","IMPRINT",EDGE,{"derivedFrom":sQuery(id+"F0.wireOp",EDGE,"E177")}),1.0]])]});
            var Q2;
            Q2=makeQuery(id+"F0.imprint","IMPRINT",FACE,{"disambiguationData":[TD([[makeQuery(id+"F0.imprint","IMPRINT",EDGE,{"derivedFrom":sQuery(id+"F0.wireOp",EDGE,"E155")}),1.0]])]});
            var Q3;
            {var subQ0=sQuery(id+"F0.wireOp",EDGE,"E109");Q3=makeQuery(id+"F0.imprint","IMPRINT",FACE,{"disambiguationData":[TD([[makeQuery(id+"F0.imprint","IMPRINT",EDGE,{"derivedFrom":subQ0}),1.0]])]});}
            var Q4;
            Q4=makeQuery(id+"F0.imprint","IMPRINT",FACE,{"disambiguationData":[TD([[makeQuery(id+"F0.imprint","IMPRINT",EDGE,{"derivedFrom":sQuery(id+"F0.wireOp",EDGE,"E197")}),-1.0]])]});
            extrude(context, id + "F1", {"entities" : qUnion([Q0, Q1, Q2, Q3, Q4]), "depth" : 10 * mm});
        }
        {
            var Q0;
            Q0=makeQuery(id+"F1.opExtrude","CAP_FACE",FACE,{"disambiguationData":[OSD([sQuery(id+"F0.wireOp",EDGE,"E0"),sQuery(id+"F0.wireOp",EDGE,"E1"),sQuery(id+"F0.wireOp",EDGE,"E2"),sQuery(id+"F0.wireOp",EDGE,"E3"),sQuery(id+"F0.wireOp",EDGE,"E4"),sQuery(id+"F0.wireOp",EDGE,"E5"),sQuery(id+"F0.wireOp",EDGE,"E6"),sQuery(id+"F0.wireOp",EDGE,"E7"),sQuery(id+"F0.wireOp",EDGE,"E8"),sQuery(id+"F0.wireOp",EDGE,"E9"),sQuery(id+"F0.wireOp",EDGE,"E10"),sQuery(id+"F0.wireOp",EDGE,"E11"),sQuery(id+"F0.wireOp",EDGE,"E12"),sQuery(id+"F0.wireOp",EDGE,"E13"),sQuery(id+"F0.wireOp",EDGE,"E14"),sQuery(id+"F0.wireOp",EDGE,"E15"),sQuery(id+"F0.wireOp",EDGE,"E16"),sQuery(id+"F0.wireOp",EDGE,"E17"),sQuery(id+"F0.wireOp",EDGE,"E18"),sQuery(id+"F0.wireOp",EDGE,"E19"),sQuery(id+"F0.wireOp",EDGE,"E20"),sQuery(id+"F0.wireOp",EDGE,"E21"),sQuery(id+"F0.wireOp",EDGE,"E22"),sQuery(id+"F0.wireOp",EDGE,"E23"),sQuery(id+"F0.wireOp",EDGE,"E24"),sQuery(id+"F0.wireOp",EDGE,"E25"),sQuery(id+"F0.wireOp",EDGE,"E26"),sQuery(id+"F0.wireOp",EDGE,"E27"),sQuery(id+"F0.wireOp",EDGE,"E28"),sQuery(id+"F0.wireOp",EDGE,"E29"),sQuery(id+"F0.wireOp",EDGE,"E30"),sQuery(id+"F0.wireOp",EDGE,"E31"),sQuery(id+"F0.wireOp",EDGE,"E32"),sQuery(id+"F0.wireOp",EDGE,"E33"),sQuery(id+"F0.wireOp",EDGE,"E34"),sQuery(id+"F0.wireOp",EDGE,"E35"),sQuery(id+"F0.wireOp",EDGE,"E36"),sQuery(id+"F0.wireOp",EDGE,"E37"),sQuery(id+"F0.wireOp",EDGE,"E38"),sQuery(id+"F0.wireOp",EDGE,"E39"),sQuery(id+"F0.wireOp",EDGE,"E40"),sQuery(id+"F0.wireOp",EDGE,"E41"),sQuery(id+"F0.wireOp",EDGE,"E42"),sQuery(id+"F0.wireOp",EDGE,"E43"),sQuery(id+"F0.wireOp",EDGE,"E44"),sQuery(id+"F0.wireOp",EDGE,"E45"),sQuery(id+"F0.wireOp",EDGE,"E46"),sQuery(id+"F0.wireOp",EDGE,"E47"),sQuery(id+"F0.wireOp",EDGE,"E48"),sQuery(id+"F0.wireOp",EDGE,"E49"),sQuery(id+"F0.wireOp",EDGE,"E50"),sQuery(id+"F0.wireOp",EDGE,"E51"),sQuery(id+"F0.wireOp",EDGE,"E52"),sQuery(id+"F0.wireOp",EDGE,"E53"),sQuery(id+"F0.wireOp",EDGE,"E54"),sQuery(id+"F0.wireOp",EDGE,"E55"),sQuery(id+"F0.wireOp",EDGE,"E56"),sQuery(id+"F0.wireOp",EDGE,"E57"),sQuery(id+"F0.wireOp",EDGE,"E58"),sQuery(id+"F0.wireOp",EDGE,"E59"),sQuery(id+"F0.wireOp",EDGE,"E60"),sQuery(id+"F0.wireOp",EDGE,"E61"),sQuery(id+"F0.wireOp",EDGE,"E62"),sQuery(id+"F0.wireOp",EDGE,"E63"),sQuery(id+"F0.wireOp",EDGE,"E64"),sQuery(id+"F0.wireOp",EDGE,"E65"),sQuery(id+"F0.wireOp",EDGE,"E66"),sQuery(id+"F0.wireOp",EDGE,"E67"),sQuery(id+"F0.wireOp",EDGE,"E68"),sQuery(id+"F0.wireOp",EDGE,"E69"),sQuery(id+"F0.wireOp",EDGE,"E70"),sQuery(id+"F0.wireOp",EDGE,"E71"),sQuery(id+"F0.wireOp",EDGE,"E72"),sQuery(id+"F0.wireOp",EDGE,"E73"),sQuery(id+"F0.wireOp",EDGE,"E74"),sQuery(id+"F0.wireOp",EDGE,"E75"),sQuery(id+"F0.wireOp",EDGE,"E76"),sQuery(id+"F0.wireOp",EDGE,"E77"),sQuery(id+"F0.wireOp",EDGE,"E78"),sQuery(id+"F0.wireOp",EDGE,"E79"),sQuery(id+"F0.wireOp",EDGE,"E80"),sQuery(id+"F0.wireOp",EDGE,"E81"),sQuery(id+"F0.wireOp",EDGE,"E82"),sQuery(id+"F0.wireOp",EDGE,"E83"),sQuery(id+"F0.wireOp",EDGE,"E84"),sQuery(id+"F0.wireOp",EDGE,"E85"),sQuery(id+"F0.wireOp",EDGE,"E86"),sQuery(id+"F0.wireOp",EDGE,"E87"),sQuery(id+"F0.wireOp",EDGE,"E88"),sQuery(id+"F0.wireOp",EDGE,"E89"),sQuery(id+"F0.wireOp",EDGE,"E90"),sQuery(id+"F0.wireOp",EDGE,"E91"),sQuery(id+"F0.wireOp",EDGE,"E92"),sQuery(id+"F0.wireOp",EDGE,"E93"),sQuery(id+"F0.wireOp",EDGE,"E94"),sQuery(id+"F0.wireOp",EDGE,"E95"),sQuery(id+"F0.wireOp",EDGE,"E96"),sQuery(id+"F0.wireOp",EDGE,"E97"),sQuery(id+"F0.wireOp",EDGE,"E98"),sQuery(id+"F0.wireOp",EDGE,"E99"),sQuery(id+"F0.wireOp",EDGE,"E100"),sQuery(id+"F0.wireOp",EDGE,"E101"),sQuery(id+"F0.wireOp",EDGE,"E102"),sQuery(id+"F0.wireOp",EDGE,"E103"),sQuery(id+"F0.wireOp",EDGE,"E104"),sQuery(id+"F0.wireOp",EDGE,"E105"),sQuery(id+"F0.wireOp",EDGE,"E106"),sQuery(id+"F0.wireOp",EDGE,"E107"),sQuery(id+"F0.wireOp",EDGE,"E108"),sQuery(id+"F0.wireOp",EDGE,"E116"),sQuery(id+"F0.wireOp",EDGE,"E117"),sQuery(id+"F0.wireOp",EDGE,"E118"),sQuery(id+"F0.wireOp",EDGE,"E119"),sQuery(id+"F0.wireOp",EDGE,"E120"),sQuery(id+"F0.wireOp",EDGE,"E121"),sQuery(id+"F0.wireOp",EDGE,"E122"),sQuery(id+"F0.wireOp",EDGE,"E123"),sQuery(id+"F0.wireOp",EDGE,"E124"),sQuery(id+"F0.wireOp",EDGE,"E125"),sQuery(id+"F0.wireOp",EDGE,"E126"),sQuery(id+"F0.wireOp",EDGE,"E127"),sQuery(id+"F0.wireOp",EDGE,"E128"),sQuery(id+"F0.wireOp",EDGE,"E129"),sQuery(id+"F0.wireOp",EDGE,"E130"),sQuery(id+"F0.wireOp",EDGE,"E131"),sQuery(id+"F0.wireOp",EDGE,"E132"),sQuery(id+"F0.wireOp",EDGE,"E133"),sQuery(id+"F0.wireOp",EDGE,"E134"),sQuery(id+"F0.wireOp",EDGE,"E135"),sQuery(id+"F0.wireOp",EDGE,"E136"),sQuery(id+"F0.wireOp",EDGE,"E137"),sQuery(id+"F0.wireOp",EDGE,"E138"),sQuery(id+"F0.wireOp",EDGE,"E139"),sQuery(id+"F0.wireOp",EDGE,"E140"),sQuery(id+"F0.wireOp",EDGE,"E141"),sQuery(id+"F0.wireOp",EDGE,"E142"),sQuery(id+"F0.wireOp",EDGE,"E143"),sQuery(id+"F0.wireOp",EDGE,"E144"),sQuery(id+"F0.wireOp",EDGE,"E145"),sQuery(id+"F0.wireOp",EDGE,"E146"),sQuery(id+"F0.wireOp",EDGE,"E147"),sQuery(id+"F0.wireOp",EDGE,"E148"),sQuery(id+"F0.wireOp",EDGE,"E149"),sQuery(id+"F0.wireOp",EDGE,"E150"),sQuery(id+"F0.wireOp",EDGE,"E151"),sQuery(id+"F0.wireOp",EDGE,"E152"),sQuery(id+"F0.wireOp",EDGE,"E153"),sQuery(id+"F0.wireOp",EDGE,"E154"),sQuery(id+"F0.wireOp",EDGE,"E172"),sQuery(id+"F0.wireOp",EDGE,"E173"),sQuery(id+"F0.wireOp",EDGE,"E174"),sQuery(id+"F0.wireOp",EDGE,"E175"),sQuery(id+"F0.wireOp",EDGE,"E176"),sQuery(id+"F0.wireOp",EDGE,"E177"),sQuery(id+"F0.wireOp",EDGE,"E178"),sQuery(id+"F0.wireOp",EDGE,"E179"),sQuery(id+"F0.wireOp",EDGE,"E180"),sQuery(id+"F0.wireOp",EDGE,"E181"),sQuery(id+"F0.wireOp",EDGE,"E182"),sQuery(id+"F0.wireOp",EDGE,"E183"),sQuery(id+"F0.wireOp",EDGE,"E184"),sQuery(id+"F0.wireOp",EDGE,"E185"),sQuery(id+"F0.wireOp",EDGE,"E186"),sQuery(id+"F0.wireOp",EDGE,"E187"),sQuery(id+"F0.wireOp",EDGE,"E188"),sQuery(id+"F0.wireOp",EDGE,"E189"),sQuery(id+"F0.wireOp",EDGE,"E190"),sQuery(id+"F0.wireOp",EDGE,"E191"),sQuery(id+"F0.wireOp",EDGE,"E192"),sQuery(id+"F0.wireOp",EDGE,"E193"),sQuery(id+"F0.wireOp",EDGE,"E194"),sQuery(id+"F0.wireOp",EDGE,"E195"),sQuery(id+"F0.wireOp",EDGE,"E196"),sQuery(id+"F0.wireOp",EDGE,"E198"),sQuery(id+"F0.wireOp",EDGE,"E199"),sQuery(id+"F0.wireOp",EDGE,"E200"),sQuery(id+"F0.wireOp",EDGE,"E201"),sQuery(id+"F0.wireOp",EDGE,"E202"),sQuery(id+"F0.wireOp",EDGE,"E203"),sQuery(id+"F0.wireOp",EDGE,"E204"),sQuery(id+"F0.wireOp",EDGE,"E205"),sQuery(id+"F0.wireOp",EDGE,"E206"),sQuery(id+"F0.wireOp",EDGE,"E207"),sQuery(id+"F0.wireOp",EDGE,"E208"),sQuery(id+"F0.wireOp",EDGE,"E209"),sQuery(id+"F0.wireOp",EDGE,"E210"),sQuery(id+"F0.wireOp",EDGE,"E211"),sQuery(id+"F0.wireOp",EDGE,"E212"),sQuery(id+"F0.wireOp",EDGE,"E213"),sQuery(id+"F0.wireOp",EDGE,"E214"),sQuery(id+"F0.wireOp",EDGE,"E215"),sQuery(id+"F0.wireOp",EDGE,"E216"),sQuery(id+"F0.wireOp",EDGE,"E217"),sQuery(id+"F0.wireOp",EDGE,"E218"),sQuery(id+"F0.wireOp",EDGE,"E219"),sQuery(id+"F0.wireOp",EDGE,"E220"),sQuery(id+"F0.wireOp",EDGE,"E221"),sQuery(id+"F0.wireOp",EDGE,"E222"),sQuery(id+"F0.wireOp",EDGE,"E223"),sQuery(id+"F0.wireOp",EDGE,"E224"),sQuery(id+"F0.wireOp",EDGE,"E225"),sQuery(id+"F0.wireOp",EDGE,"E226"),sQuery(id+"F0.wireOp",EDGE,"E227"),sQuery(id+"F0.wireOp",EDGE,"E228"),sQuery(id+"F0.wireOp",EDGE,"E229"),sQuery(id+"F0.wireOp",EDGE,"E230"),sQuery(id+"F0.wireOp",EDGE,"E231"),sQuery(id+"F0.wireOp",EDGE,"E232"),sQuery(id+"F0.wireOp",EDGE,"E233"),sQuery(id+"F0.wireOp",EDGE,"E234"),sQuery(id+"F0.wireOp",EDGE,"E235"),sQuery(id+"F0.wireOp",EDGE,"E236"),sQuery(id+"F0.wireOp",EDGE,"E237"),sQuery(id+"F0.wireOp",EDGE,"E238"),sQuery(id+"F0.wireOp",EDGE,"E239"),sQuery(id+"F0.wireOp",EDGE,"E240"),sQuery(id+"F0.wireOp",EDGE,"E241"),sQuery(id+"F0.wireOp",EDGE,"E242"),sQuery(id+"F0.wireOp",EDGE,"E243"),sQuery(id+"F0.wireOp",EDGE,"E244"),sQuery(id+"F0.wireOp",EDGE,"E245"),sQuery(id+"F0.wireOp",EDGE,"E246"),sQuery(id+"F0.wireOp",EDGE,"E247"),sQuery(id+"F0.wireOp",EDGE,"E248"),sQuery(id+"F0.wireOp",EDGE,"E249"),sQuery(id+"F0.wireOp",EDGE,"E250"),sQuery(id+"F0.wireOp",EDGE,"E251"),sQuery(id+"F0.wireOp",EDGE,"E252"),sQuery(id+"F0.wireOp",EDGE,"E253"),sQuery(id+"F0.wireOp",EDGE,"E254"),sQuery(id+"F0.wireOp",EDGE,"E255"),sQuery(id+"F0.wireOp",EDGE,"E257"),sQuery(id+"F0.wireOp",EDGE,"E258"),sQuery(id+"F0.wireOp",EDGE,"E259"),sQuery(id+"F0.wireOp",EDGE,"E260"),sQuery(id+"F0.wireOp",EDGE,"E261"),sQuery(id+"F0.wireOp",EDGE,"E262"),sQuery(id+"F0.wireOp",EDGE,"E263"),sQuery(id+"F0.wireOp",EDGE,"E264"),sQuery(id+"F0.wireOp",EDGE,"E265"),sQuery(id+"F0.wireOp",EDGE,"E266"),sQuery(id+"F0.wireOp",EDGE,"E267"),sQuery(id+"F0.wireOp",EDGE,"E268"),sQuery(id+"F0.wireOp",EDGE,"E269"),sQuery(id+"F0.wireOp",EDGE,"E270"),sQuery(id+"F0.wireOp",EDGE,"E271"),sQuery(id+"F0.wireOp",EDGE,"E272"),sQuery(id+"F0.wireOp",EDGE,"E273"),sQuery(id+"F0.wireOp",EDGE,"E274"),sQuery(id+"F0.wireOp",EDGE,"E275"),sQuery(id+"F0.wireOp",EDGE,"E276"),sQuery(id+"F0.wireOp",EDGE,"E277"),sQuery(id+"F0.wireOp",EDGE,"E278"),sQuery(id+"F0.wireOp",EDGE,"E279"),sQuery(id+"F0.wireOp",EDGE,"E280"),sQuery(id+"F0.wireOp",EDGE,"E281"),sQuery(id+"F0.wireOp",EDGE,"E282"),sQuery(id+"F0.wireOp",EDGE,"E283"),sQuery(id+"F0.wireOp",EDGE,"E284"),sQuery(id+"F0.wireOp",EDGE,"E285"),sQuery(id+"F0.wireOp",EDGE,"E286"),sQuery(id+"F0.wireOp",EDGE,"E287"),sQuery(id+"F0.wireOp",EDGE,"E288"),sQuery(id+"F0.wireOp",EDGE,"E289"),sQuery(id+"F0.wireOp",EDGE,"E290"),sQuery(id+"F0.wireOp",EDGE,"E291"),sQuery(id+"F0.wireOp",EDGE,"E292"),sQuery(id+"F0.wireOp",EDGE,"E293"),sQuery(id+"F0.wireOp",EDGE,"E294"),sQuery(id+"F0.wireOp",EDGE,"E295"),sQuery(id+"F0.wireOp",EDGE,"E296"),sQuery(id+"F0.wireOp",EDGE,"E297"),sQuery(id+"F0.wireOp",EDGE,"E298"),sQuery(id+"F0.wireOp",EDGE,"E299"),sQuery(id+"F0.wireOp",EDGE,"E300"),sQuery(id+"F0.wireOp",EDGE,"E301"),sQuery(id+"F0.wireOp",EDGE,"E302"),sQuery(id+"F0.wireOp",EDGE,"E303"),sQuery(id+"F0.wireOp",EDGE,"E304")])],"isStart":false});
            shell(context, id + "F2", {"entities" : qUnion([Q0]), "thickness" : 1 * mm, "oppositeDirection" : true});
        }
    });
